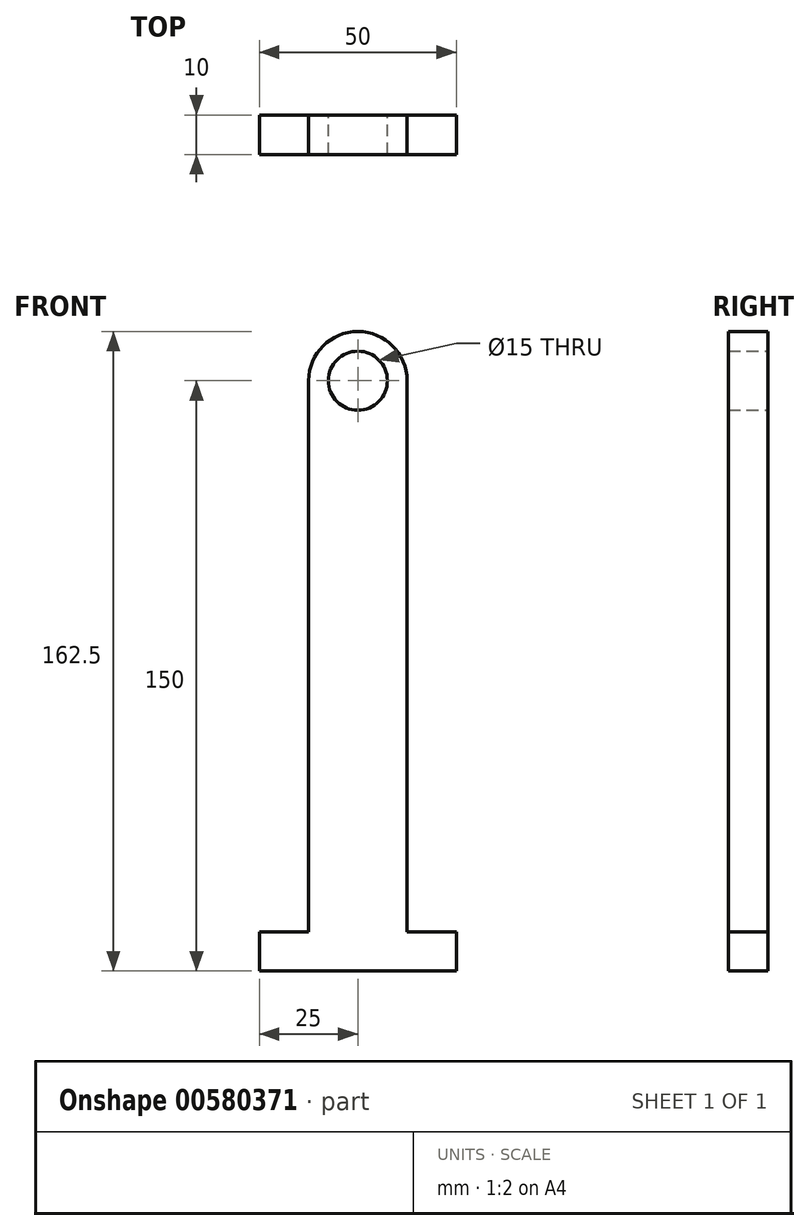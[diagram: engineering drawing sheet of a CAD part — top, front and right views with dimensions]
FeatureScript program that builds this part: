
annotation { "Feature Type Name" : "Feature", "Feature Type Description" : "" }
export const myFeature = defineFeature(function(context is Context, id is Id, definition is map)
    precondition{}
    {
        {
            var Q0;
            Q0=qCreatedBy(makeId("Front.planeOp"),FACE);
            var sketch = newSketch(context, id + "F0", { "sketchPlane" : qUnion([Q0])});
            skLineSegment(sketch, "E0", {"start": v(0, 0) * mm, "end": v(0, 150) * mm, "construction": true});
            skArc(sketch, "E1", {"start": v(12.5, 150) * mm, "mid": v(0, 162.5) * mm, "end": v(-12.5, 150) * mm});
            skCircle(sketch, "E2", {"center": v(0, 150) * mm, "radius": 7.5 * mm});
            skLineSegment(sketch, "E3", {"start": v(-12.5, 150) * mm, "end": v(-12.5, 10) * mm});
            skLineSegment(sketch, "E4.MirrorCS", {"start": v(12.5, 150) * mm, "end": v(12.5, 10) * mm});
            skLineSegment(sketch, "E5", {"start": v(-12.5, 0) * mm, "end": v(12.5, 0) * mm});
            skLineSegment(sketch, "E6.bottom", {"start": v(-25, 0) * mm, "end": v(25, 0) * mm});
            skLineSegment(sketch, "E6.top", {"start": v(-25, 10) * mm, "end": v(-12.5, 10) * mm});
            skLineSegment(sketch, "E6.left", {"start": v(-25, 0) * mm, "end": v(-25, 10) * mm});
            skLineSegment(sketch, "E6.right", {"start": v(25, 0) * mm, "end": v(25, 10) * mm});
            skLineSegment(sketch, "E7.trimOffspring", {"start": v(12.5, 10) * mm, "end": v(25, 10) * mm});
            skSolve(sketch);
        }
        {
            var Q0;
            Q0=makeQuery(id+"F0.imprint","IMPRINT",FACE,{"disambiguationData":[TD([[makeQuery(id+"F0.imprint","IMPRINT",EDGE,{"derivedFrom":sQuery(id+"F0.wireOp",EDGE,"E1")}),1.0]])]});
            extrude(context, id + "F1", {"entities" : qUnion([Q0]), "depth" : 10 * mm, "offsetDistance" : 25 * mm});
        }
    });
